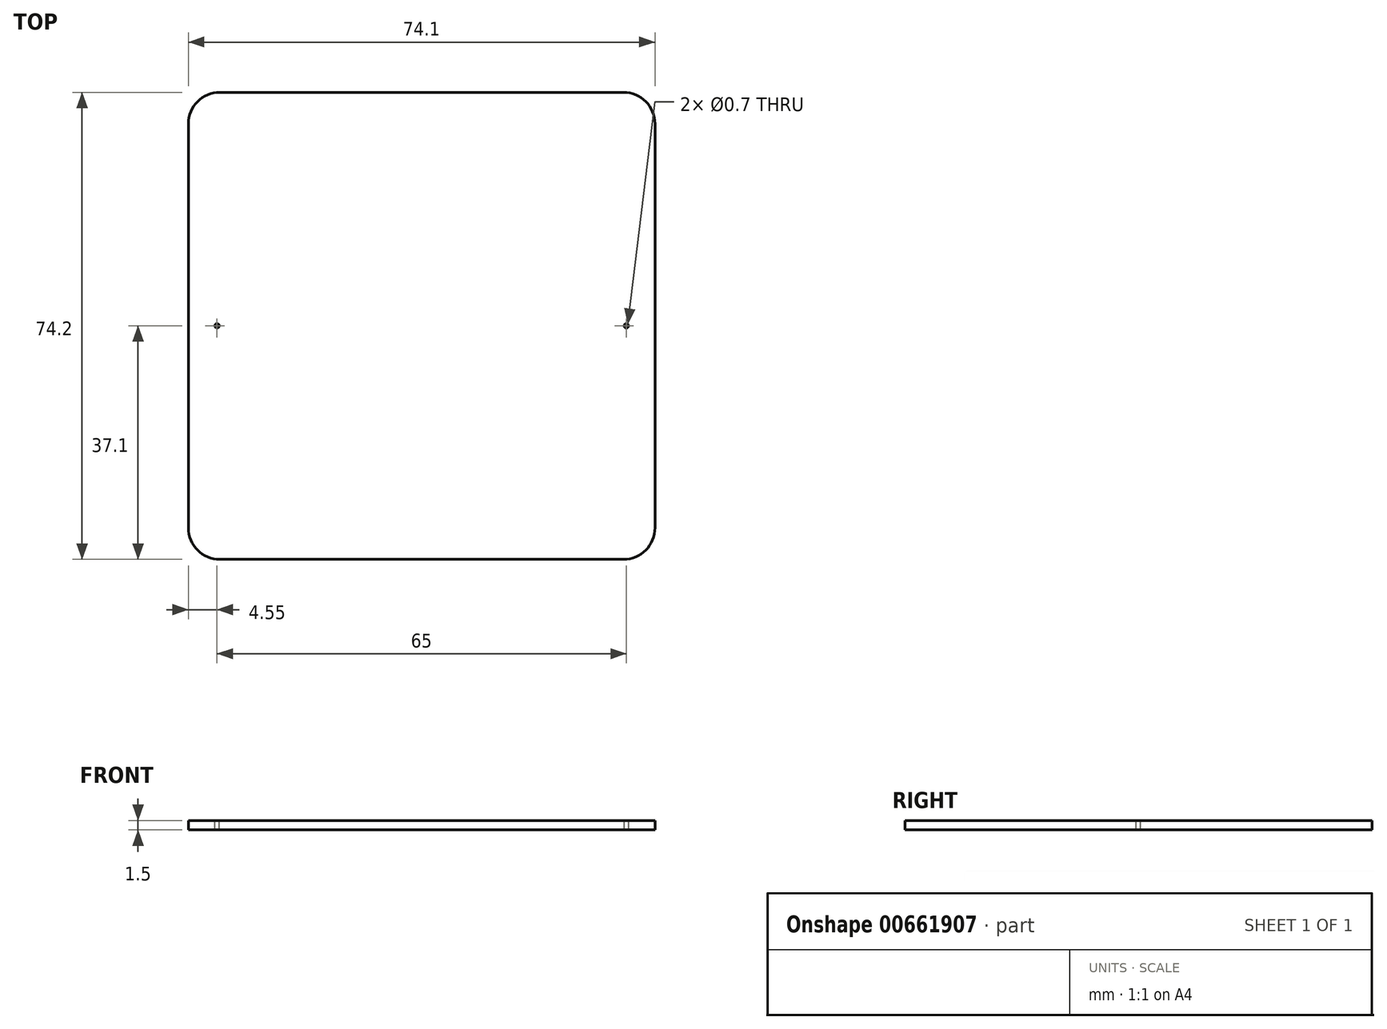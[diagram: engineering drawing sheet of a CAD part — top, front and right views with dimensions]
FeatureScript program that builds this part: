
annotation { "Feature Type Name" : "Feature", "Feature Type Description" : "" }
export const myFeature = defineFeature(function(context is Context, id is Id, definition is map)
    precondition{}
    {
        {
            var Q0;
            Q0=qCreatedBy(makeId("Top.planeOp"),FACE);
            var sketch = newSketch(context, id + "F0", { "sketchPlane" : qUnion([Q0])});
            skLineSegment(sketch, "E0.bottom", {"start": v(0, 0) * mm, "end": v(74.1, 0) * mm});
            skLineSegment(sketch, "E0.top", {"start": v(0, 74.2) * mm, "end": v(74.1, 74.2) * mm});
            skLineSegment(sketch, "E0.left", {"start": v(0, 0) * mm, "end": v(0, 74.2) * mm});
            skLineSegment(sketch, "E0.right", {"start": v(74.1, 0) * mm, "end": v(74.1, 74.2) * mm});
            skCircle(sketch, "E1", {"center": v(4.55, 37.1) * mm, "radius": 2.62 * mm});
            skPoint(sketch, "E1.centerSnap0", {"position": v(0, 37.1) * mm});
            skCircle(sketch, "E2", {"center": v(69.55, 37.1) * mm, "radius": 2.62 * mm});
            skPoint(sketch, "E2.centerSnap0", {"position": v(74.1, 37.1) * mm});
            skSolve(sketch);
        }
        {
            var Q0;
            Q0=makeQuery(id+"F0.imprint","IMPRINT",FACE,{"disambiguationData":[TD([[makeQuery(id+"F0.imprint","IMPRINT",EDGE,{"derivedFrom":sQuery(id+"F0.wireOp",EDGE,"E0.bottom")}),1.0]])]});
            var Q1;
            Q1=makeQuery(id+"F0.imprint","IMPRINT",FACE,{"disambiguationData":[TD([[makeQuery(id+"F0.imprint","IMPRINT",EDGE,{"derivedFrom":sQuery(id+"F0.wireOp",EDGE,"E1")}),1.0]])]});
            var Q2;
            Q2=makeQuery(id+"F0.imprint","IMPRINT",FACE,{"disambiguationData":[TD([[makeQuery(id+"F0.imprint","IMPRINT",EDGE,{"derivedFrom":sQuery(id+"F0.wireOp",EDGE,"E2")}),1.0]])]});
            extrude(context, id + "F1", {"entities" : qUnion([Q0, Q1, Q2]), "depth" : 1.5 * mm, "offsetDistance" : 25 * mm});
        }
        {
            var Q0;
            Q0=makeQuery(id+"F1.opExtrude","CAP_FACE",FACE,{"disambiguationData":[OSD([sQuery(id+"F0.wireOp",EDGE,"E0.bottom"),sQuery(id+"F0.wireOp",EDGE,"E0.top"),sQuery(id+"F0.wireOp",EDGE,"E0.left"),sQuery(id+"F0.wireOp",EDGE,"E0.right")])],"isStart":false});
            var sketch = newSketch(context, id + "F2", { "sketchPlane" : qUnion([Q0])});
            skCircle(sketch, "E3", {"center": v(4.55, 37.1) * mm, "radius": 0.35 * mm});
            skCircle(sketch, "E4", {"center": v(69.55, 37.1) * mm, "radius": 0.35 * mm});
            skSolve(sketch);
        }
        {
            var Q0;
            Q0=makeQuery(id+"F2.imprint","IMPRINT",FACE,{"disambiguationData":[TD([[makeQuery(id+"F2.imprint","IMPRINT",EDGE,{"derivedFrom":sQuery(id+"F2.wireOp",EDGE,"E3")}),1.0]])]});
            var Q1;
            Q1=makeQuery(id+"F2.imprint","IMPRINT",FACE,{"disambiguationData":[TD([[makeQuery(id+"F2.imprint","IMPRINT",EDGE,{"derivedFrom":sQuery(id+"F2.wireOp",EDGE,"E4")}),1.0]])]});
            extrude(context, id + "F3", {"entities" : qUnion([Q0, Q1]), "operationType" : NewBodyOperationType.REMOVE, "endBound" : BoundingType.THROUGH_ALL, "oppositeDirection" : true, "depth" : 25 * mm, "offsetDistance" : 25 * mm});
        }
        {
            var Q0;
            Q0=makeQuery(id+"F1.opExtrude","SWEPT_EDGE",EDGE,{"disambiguationData":[OSD([sQuery(id+"F0.wireOp",EDGE,"E0.top"),sQuery(id+"F0.wireOp",EDGE,"E0.right")])]});
            var Q1;
            Q1=makeQuery(id+"F1.opExtrude","SWEPT_EDGE",EDGE,{"disambiguationData":[OSD([sQuery(id+"F0.wireOp",EDGE,"E0.top"),sQuery(id+"F0.wireOp",EDGE,"E0.left")])]});
            var Q2;
            Q2=makeQuery(id+"F1.opExtrude","SWEPT_EDGE",EDGE,{"disambiguationData":[OSD([sQuery(id+"F0.wireOp",EDGE,"E0.bottom"),sQuery(id+"F0.wireOp",EDGE,"E0.left")])]});
            var Q3;
            Q3=makeQuery(id+"F1.opExtrude","SWEPT_EDGE",EDGE,{"disambiguationData":[OSD([sQuery(id+"F0.wireOp",EDGE,"E0.bottom"),sQuery(id+"F0.wireOp",EDGE,"E0.right")])]});
            fillet(context, id + "F4", {"entities" : qUnion([Q0, Q1, Q2, Q3]), "radius" : 5 * mm, "tangentPropagation" : true, "allowEdgeOverflow" : false});
        }
    });
